# Revit family: Monomando de Lavabo PIU-100
name_source: partatom
category: Plumbing Fixtures
revit_build: Autodesk Revit 2015 (Build: 20140223_1515(x64)
units: mm (PartAtom-declared; Revit-internal decimal feet)

## types (1)
- Monomando de Lavabo PIU-100
    Accesorios = Desagüe de push, Llave allen 5/64", Llave para aireador, Llave de mantenimiento, Mangueras flexibles.
    Características del Producto = Monomando con Desagüe de Push
    Cuerpo de Latón = Brass
    Default Elevation = 1"
    Description = Monomando para lavabo con desagüe de push.
    Garantía = El producto HELVEX está garantizado como libre de defectos en materiales y procesos de fabricación. El producto HELVEX está garantizado, en lo que se refiere a los acabados; por un periodo de 10 años en los acabados cromo y duravex, y por 2 años en acabados diferentes al cromo, a partir de la fecha de compra indicada en la factura
    Instalación = Conexión ½ - 14 NPSM
    Manufacturer = HELVEX S.A. de C.V.
    Model = PIU-100
    Operación = Para abrir el flujo de agua deslice el maneral hacia atrás, para regular la temperatura, gire a la izquierda para calentar y a la derecha para enfriar.
    Presión Máxima de Trabajo = 85.3 psi
    Presión Mínima de Trabajo = 2.8 psi
    Total Depth = 8"
    Total Height = 8"
    Total Width = 5"
    Type Image = PIU-100.jpg
    URL = http://www.helvex.com.mx

## geometry (parser evidence)
native form markers: Sweep x3
no freeform markers — native parametric forms only
